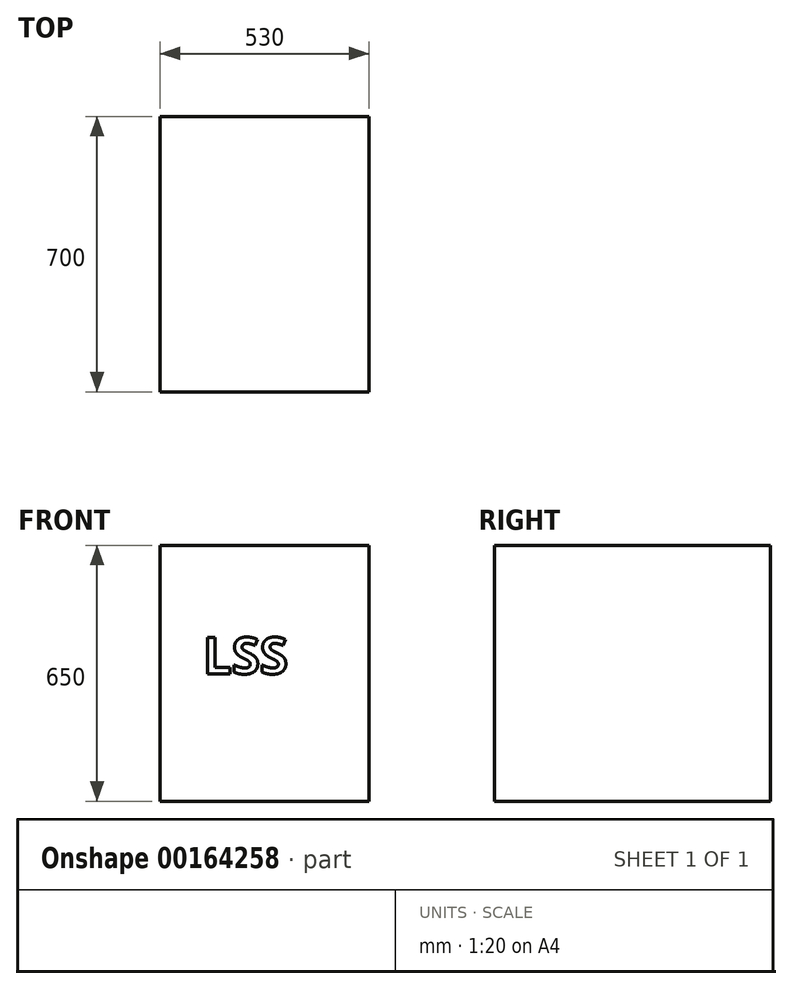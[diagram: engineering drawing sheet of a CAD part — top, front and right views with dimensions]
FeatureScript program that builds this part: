
annotation { "Feature Type Name" : "Feature", "Feature Type Description" : "" }
export const myFeature = defineFeature(function(context is Context, id is Id, definition is map)
    precondition{}
    {
        {
            var Q0;
            Q0=qCreatedBy(makeId("Top.planeOp"),FACE);
            var sketch = newSketch(context, id + "F0", { "sketchPlane" : qUnion([Q0])});
            skLineSegment(sketch, "E0.bottom", {"start": v(-274.15, 447.59) * mm, "end": v(255.85, 447.59) * mm});
            skLineSegment(sketch, "E0.top", {"start": v(-274.15, -252.41) * mm, "end": v(255.85, -252.41) * mm});
            skLineSegment(sketch, "E0.left", {"start": v(-274.15, 447.59) * mm, "end": v(-274.15, -252.41) * mm});
            skLineSegment(sketch, "E0.right", {"start": v(255.85, 447.59) * mm, "end": v(255.85, -252.41) * mm});
            skSolve(sketch);
        }
        {
            var Q0;
            Q0 = qSketchRegion(id + "F0", true);
            extrude(context, id + "F1", {"entities" : qUnion([Q0]), "depth" : 650 * mm});
        }
        {
            var Q0;
            Q0=makeQuery(id+"F1.opExtrude","SWEPT_FACE",FACE,{"disambiguationData":[OSD([sQuery(id+"F0.wireOp",EDGE,"E0.top")])]});
            var sketch = newSketch(context, id + "F2", { "sketchPlane" : qUnion([Q0])});
            skText(sketch, "E1", { "text": "LSS", "fontName": "OpenSans-Bold.ttf"});
            const initialGuessF2  = {"E1": [-0.16525, 0.32348, 1, 0, 0.09319]};
            skSetInitialGuess(sketch, initialGuessF2);
            skSolve(sketch);
        }
        {
            var Q0;
            Q0 = qSketchRegion(id + "F2", true);
            extrude(context, id + "F3", {"entities" : qUnion([Q0]), "operationType" : NewBodyOperationType.REMOVE, "oppositeDirection" : true, "depth" : 1 * mm});
        }
    });
